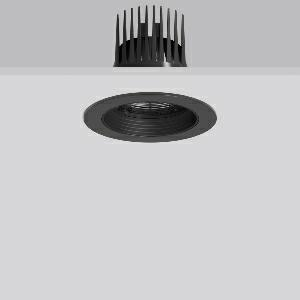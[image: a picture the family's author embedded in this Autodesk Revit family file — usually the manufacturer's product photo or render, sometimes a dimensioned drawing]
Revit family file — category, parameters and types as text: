
# Revit family: heledon_maxi_e_901767_003_2_f1a8
name_source: partatom
category: Lighting Fixtures
units: mm (PartAtom-declared; Revit-internal decimal feet)

## family parameters
Cut with Voids When Loaded = No
Host = Face
Light Source = No
Part Type = Normal
Room Calculation Point = No
Round Connector Dimension = Use Diameter
Shared = No

## types (1)
- HELEDON maxi E (1 x LED Modul 927, 3500 lm, 2700)
    Apparent Load = 35 VA
    Approval mark = CE
    CIE Flux Codes = 97 100 100 100 100
    Color Rendering = 92
    Color Temperature = 2700
    Default Elevation = 1800 mm
    Description = Series: HELEDON maxi
Round recessed downlight. Housing: die-cast aluminium, powder-coated. Black plastic ring and recessed LED to prevent glare from the side. Optical assembly with lens made of plastic (polycarbonate) for the best homogeneous light distribution - can be changed without tools. Best colour rendering index Ra>90. Suitable for Recessed ceiling mounting. Installation without tools thanks to spring fastening system. Including separate LED converter with connecting cable 600 mm.High quality converter without flickering and stroboscopic effect. Through-wiring box (5 pole) available as accessory. The following accessories can be mounted without use of tools: interchangeable lenses, decorative glasses, honeycomb louvre, clear and frosted diffusers, white interchangeable plastic ring. 
Colour: deep black, matt (RAL 9005)
Diameter: 162 mm
Height: 3 mm
Cut-out diameter: 152 mm
Recess height: 200 mm
Luminaire: recess height: 135 mm
Lamp: LED
Socket: without socket
Colour temperature: 2700K
Colour rendering index (CRI): 92
System power: 35 W
Rated luminous flux: 3500 lm
Luminous efficiency: 100 lm/W
Control gear: Regulated power supply
Protection class: II
Type of protection: IP 20
    Height = 0 mm  [stored 0 ft]
    Lamp = 1 x LED Modul 927
    Lamp Light Flux = 3500 lm
    Lamp count = 1
    Length = 162 mm
    Lifetime = 50000 h
    Luminous efficacy = 100 lm/W
    Manufacturer = RZB
    ModVariant = No
    Model = 901767.003.2
    Mounting Place = Ceiling
    Mounting Type = Recessed
    Number of Poles = 1
    OnlyDefault = Yes
    Power Factor = 1
    Product Name = HELEDON maxi E
    Product group = Recessed downlights
    ProductGroupID = 402
    Protection Class = Protection class II
    Protection Degree = IP 20
    RLX_Detail_Level = 1
    RLX_Emergency_Light_Flux = 0 lm
    RLX_Emergency_Type = 0
    RLX_Emergency_Type_DB = No
    RlxData = <blob elided: 120001 chars, md5=2b4c6d10>
    Socket = socket
    Standby Power = 0 W
    System Light Flux = 3500 lm
    System Power = 35 W
    Type Comments = Product without accessories
    Type Image = 901663.003.jpg
    URL = http://relux.com
    VarID = ---
    Voltage = 230 V
    Voltage Range = 220-240 V
    Weight = 0.00 kg
    Width = 0 mm  [stored 0 ft]

note: [stored X ft] marks values corroborated as IEEE doubles in the binary element streams (Revit-internal decimal feet)

## geometry (parser evidence)
native form markers: Blend x4, Sweep x12
no freeform markers — native parametric forms only
